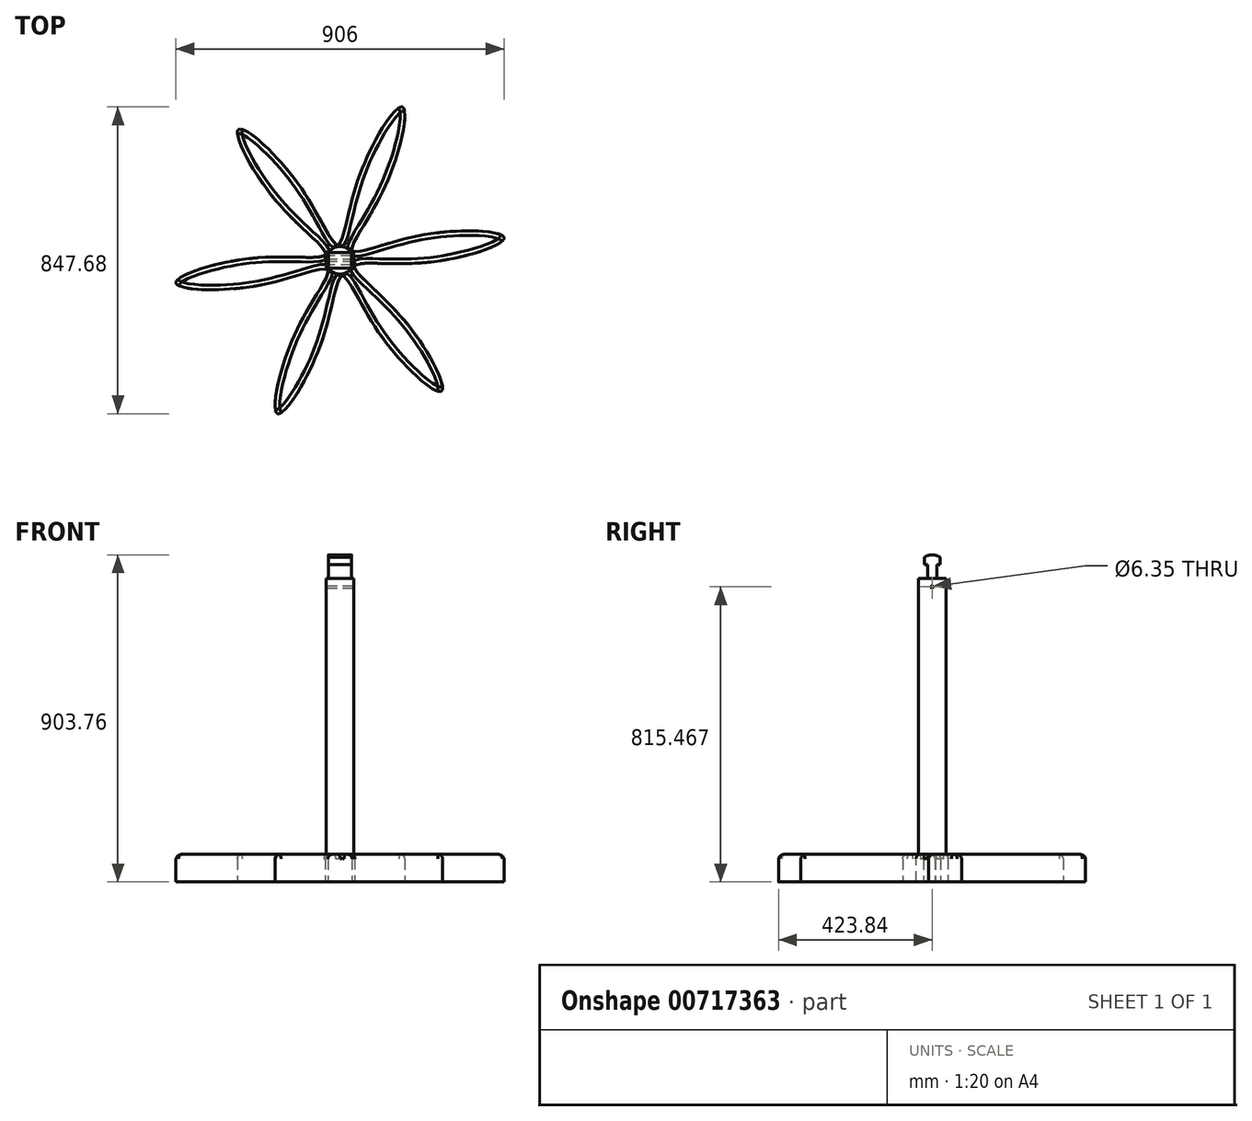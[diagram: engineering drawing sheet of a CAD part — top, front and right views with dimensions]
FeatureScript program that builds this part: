
annotation { "Feature Type Name" : "Feature", "Feature Type Description" : "" }
export const myFeature = defineFeature(function(context is Context, id is Id, definition is map)
    precondition{}
    {
        {
            var Q0;
            Q0=qCreatedBy(makeId("Top.planeOp"),FACE);
            var sketch = newSketch(context, id + "F0", { "sketchPlane" : qUnion([Q0])});
            skCircle(sketch, "E0", {"center": v(0, 0) * mm, "radius": 38.1 * mm});
            skSolve(sketch);
        }
        {
            var Q0;
            Q0=makeQuery(id+"F0.imprint","IMPRINT",FACE,{"disambiguationData":[TD([[makeQuery(id+"F0.imprint","IMPRINT",EDGE,{"derivedFrom":sQuery(id+"F0.wireOp",EDGE,"E0")}),1.0]])]});
            extrude(context, id + "F1", {"entities" : qUnion([Q0]), "depth" : 762 * mm, "offsetDistance" : 25.4 * mm});
        }
        {
            var Q0;
            Q0=makeQuery(id+"F1.opExtrude","CAP_FACE",FACE,{"disambiguationData":[OSD([sQuery(id+"F0.wireOp",EDGE,"E0")])],"isStart":false});
            var sketch = newSketch(context, id + "F2", { "sketchPlane" : qUnion([Q0])});
            skLineSegment(sketch, "E1", {"start": v(-31.75, 21.06) * mm, "end": v(-31.75, -21.06) * mm, "construction": true});
            skLineSegment(sketch, "E2", {"start": v(31.75, 21.06) * mm, "end": v(31.75, -21.06) * mm, "construction": true});
            skLineSegment(sketch, "E3", {"start": v(-31.9, 50.8) * mm, "end": v(-31.75, -50.8) * mm});
            skLineSegment(sketch, "E4", {"start": v(31.91, 50.8) * mm, "end": v(31.91, -50.8) * mm});
            skLineSegment(sketch, "E5", {"start": v(-31.9, 50.8) * mm, "end": v(31.91, 50.8) * mm});
            skLineSegment(sketch, "E6", {"start": v(31.91, -50.8) * mm, "end": v(-31.75, -50.8) * mm});
            skSolve(sketch);
        }
        {
            var Q0;
            {var subQ0=sQuery(id+"F2.wireOp",EDGE,"E5");var subQ1=sQuery(id+"F2.wireOp",EDGE,"E3");var subQ2=makeQuery(id+"F2.imprint","INTERSECT",VERTEX,{"derivedFrom":[subQ1,subQ0]});Q0=makeQuery(id+"F2.imprint","IMPRINT",FACE,{"disambiguationData":[TD([[makeQuery(id+"F2.imprint","IMPRINT",EDGE,{"disambiguationData":[TD([[subQ2,-1.0]])],"derivedFrom":subQ1}),1.0]])]});}
            var Q1;
            {var subQ0=sQuery(id+"F2.wireOp",EDGE,"E5");var subQ1=sQuery(id+"F2.wireOp",EDGE,"E4");var subQ2=makeQuery(id+"F2.imprint","INTERSECT",VERTEX,{"derivedFrom":[subQ1,subQ0]});Q1=makeQuery(id+"F2.imprint","IMPRINT",FACE,{"disambiguationData":[TD([[makeQuery(id+"F2.imprint","IMPRINT",EDGE,{"disambiguationData":[TD([[subQ2,-1.0]])],"derivedFrom":subQ1}),-1.0]])]});}
            var Q2;
            {var subQ1=makeQuery(id+"F1.opExtrude","CAP_EDGE",EDGE,{"disambiguationData":[OSD([sQuery(id+"F0.wireOp",EDGE,"E0")])],"isStart":false});var subQ7=sQuery(id+"F2.wireOp",EDGE,"E3");var subQ8=makeQuery(id+"F2.imprint","INTERSECT",VERTEX,{"disambiguationData":[OD(0.0)],"derivedFrom":[subQ1,subQ7]});Q2=makeQuery(id+"F2.imprint","IMPRINT",FACE,{"disambiguationData":[TD([[makeQuery(id+"F2.imprint","IMPRINT",EDGE,{"disambiguationData":[TD([[subQ8,-1.0]])],"derivedFrom":subQ7}),1.0]])]});}
            var Q3;
            {var subQ0=sQuery(id+"F2.wireOp",EDGE,"E6");var subQ1=sQuery(id+"F2.wireOp",EDGE,"E3");var subQ2=makeQuery(id+"F2.imprint","INTERSECT",VERTEX,{"derivedFrom":[subQ1,subQ0]});Q3=makeQuery(id+"F2.imprint","IMPRINT",FACE,{"disambiguationData":[TD([[makeQuery(id+"F2.imprint","IMPRINT",EDGE,{"disambiguationData":[TD([[subQ2,1.0]])],"derivedFrom":subQ1}),1.0]])]});}
            var Q4;
            {var subQ0=sQuery(id+"F2.wireOp",EDGE,"E6");var subQ1=sQuery(id+"F2.wireOp",EDGE,"E4");var subQ2=makeQuery(id+"F2.imprint","INTERSECT",VERTEX,{"derivedFrom":[subQ1,subQ0]});Q4=makeQuery(id+"F2.imprint","IMPRINT",FACE,{"disambiguationData":[TD([[makeQuery(id+"F2.imprint","IMPRINT",EDGE,{"disambiguationData":[TD([[subQ2,1.0]])],"derivedFrom":subQ1}),-1.0]])]});}
            extrude(context, id + "F3", {"entities" : qUnion([Q0, Q1, Q2, Q3, Q4]), "operationType" : NewBodyOperationType.ADD, "depth" : 101.6 * mm, "offsetDistance" : 25.4 * mm});
        }
        {
            var Q0;
            Q0=makeQuery(id+"F3.opExtrude","SWEPT_FACE",FACE,{"disambiguationData":[OSD([sQuery(id+"F2.wireOp",EDGE,"E3")])]});
            var sketch = newSketch(context, id + "F4", { "sketchPlane" : qUnion([Q0])});
            skLineSegment(sketch, "E7", {"start": v(-12.75, 762) * mm, "end": v(12.65, 762) * mm, "construction": true});
            skLineSegment(sketch, "E8", {"start": v(-12.75, 762) * mm, "end": v(-12.75, 800.1) * mm});
            skLineSegment(sketch, "E9", {"start": v(12.65, 762) * mm, "end": v(12.65, 800.1) * mm});
            skLineSegment(sketch, "E10", {"start": v(-12.75, 800.1) * mm, "end": v(-38.15, 800.1) * mm});
            skLineSegment(sketch, "E11", {"start": v(12.65, 800.1) * mm, "end": v(38.05, 800.1) * mm});
            skArc(sketch, "E12", {"start": v(38.05, 800.1) * mm, "mid": v(-0.05, 827.56) * mm, "end": v(-38.15, 800.1) * mm});
            skLineSegment(sketch, "E13", {"start": v(-12.75, 762) * mm, "end": v(-63.55, 762) * mm});
            skLineSegment(sketch, "E14", {"start": v(12.65, 762) * mm, "end": v(63.45, 762) * mm});
            skLineSegment(sketch, "E15", {"start": v(-63.55, 762) * mm, "end": v(-63.55, 838.2) * mm});
            skLineSegment(sketch, "E16", {"start": v(63.45, 762) * mm, "end": v(63.45, 838.2) * mm});
            skLineSegment(sketch, "E17", {"start": v(-63.55, 838.2) * mm, "end": v(63.45, 838.2) * mm});
            skSolve(sketch);
        }
        {
            var Q0;
            {var subQ8=sQuery(id+"F4.wireOp",EDGE,"E8");Q0=makeQuery(id+"F4.imprint","IMPRINT",FACE,{"disambiguationData":[TD([[makeQuery(id+"F4.imprint","IMPRINT",EDGE,{"derivedFrom":subQ8}),1.0]])]});}
            extrude(context, id + "F5", {"entities" : qUnion([Q0]), "operationType" : NewBodyOperationType.REMOVE, "oppositeDirection" : true, "depth" : 76.2 * mm, "offsetDistance" : 25.4 * mm});
        }
        {
            var Q0;
            Q0=makeQuery(id+"F3.opExtrude","SWEPT_FACE",FACE,{"disambiguationData":[OSD([sQuery(id+"F2.wireOp",EDGE,"E6")])]});
            extrude(context, id + "F6", {"entities" : qUnion([Q0]), "operationType" : NewBodyOperationType.REMOVE, "oppositeDirection" : true, "depth" : 6.35 * mm, "offsetDistance" : 25.4 * mm});
        }
        {
            var Q0;
            Q0=makeQuery(id+"F5.boolean.opBoolean","SPLIT",FACE,{"disambiguationData":[TD([makeQuery(id+"F1.opExtrude","CAP_FACE",FACE,{"disambiguationData":[OSD([sQuery(id+"F0.wireOp",EDGE,"E0")])],"isStart":false})])],"derivedFrom":makeQuery(id+"F3.opExtrude","SWEPT_FACE",FACE,{"disambiguationData":[OSD([sQuery(id+"F2.wireOp",EDGE,"E4")])]})});
            var sketch = newSketch(context, id + "F7", { "sketchPlane" : qUnion([Q0])});
            skLineSegment(sketch, "E18", {"start": v(21.7, 821.26) * mm, "end": v(21.7, 800.1) * mm});
            skLineSegment(sketch, "E19", {"start": v(-21.49, 821.26) * mm, "end": v(-21.49, 800.1) * mm, "construction": true});
            skLineSegment(sketch, "E20.bottom", {"start": v(-21.62, 960.65) * mm, "end": v(-49.27, 960.65) * mm});
            skLineSegment(sketch, "E20.top", {"start": v(-21.62, 921.94) * mm, "end": v(-49.27, 921.94) * mm});
            skLineSegment(sketch, "E20.left", {"start": v(-21.62, 960.65) * mm, "end": v(-21.62, 921.94) * mm});
            skLineSegment(sketch, "E20.right", {"start": v(-49.27, 960.65) * mm, "end": v(-49.27, 921.94) * mm});
            skSolve(sketch);
        }
        {
            var Q0;
            {var subQ8=sQuery(id+"F7.wireOp",EDGE,"E20.bottom");Q0=makeQuery(id+"F7.imprint","IMPRINT",FACE,{"disambiguationData":[TD([[makeQuery(id+"F7.imprint","IMPRINT",EDGE,{"derivedFrom":subQ8}),1.0]])]});}
            var Q1;
            {var subQ0=sQuery(id+"F7.wireOp",EDGE,"E20.left");var subQ1=makeQuery(id+"F3.opExtrude","SWEPT_FACE",FACE,{"disambiguationData":[OSD([sQuery(id+"F2.wireOp",EDGE,"E4")])]});var subQ2=makeQuery(id+"F5.boolean.opBoolean","INTERSECT",EDGE,{"derivedFrom":[subQ1,makeQuery(id+"F5.opExtrude","SWEPT_FACE",FACE,{"disambiguationData":[OSD([sQuery(id+"F4.wireOp",EDGE,"E12")])]})]});var subQ3=makeQuery(id+"F7.imprint","INTERSECT",VERTEX,{"derivedFrom":[subQ2,subQ0]});Q1=makeQuery(id+"F7.imprint","IMPRINT",FACE,{"disambiguationData":[TD([[makeQuery(id+"F7.imprint","IMPRINT",EDGE,{"disambiguationData":[TD([[subQ3,-1.0]])],"derivedFrom":subQ0}),-1.0]])]});}
            var Q2;
            {var subQ0=sQuery(id+"F7.wireOp",EDGE,"E18");Q2=makeQuery(id+"F7.imprint","IMPRINT",FACE,{"disambiguationData":[TD([[makeQuery(id+"F7.imprint","IMPRINT",EDGE,{"derivedFrom":subQ0}),1.0]])]});}
            extrude(context, id + "F8", {"entities" : qUnion([Q0, Q1, Q2]), "operationType" : NewBodyOperationType.REMOVE, "oppositeDirection" : true, "depth" : 127 * mm, "offsetDistance" : 25.4 * mm});
        }
        {
            var Q0;
            {var subQ0=sQuery(id+"F0.wireOp",EDGE,"E0");var subQ2=sQuery(id+"F2.wireOp",EDGE,"E4");var subQ3=sQuery(id+"F2.wireOp",EDGE,"E3");var subQ5=makeQuery(id+"F1.opExtrude","CAP_FACE",FACE,{"disambiguationData":[OSD([subQ0])],"isStart":false});Q0=makeQuery(id+"F5.boolean.opBoolean","MERGE",FACE,{"derivedFrom":[makeQuery(id+"F3.boolean.opBoolean","SPLIT",FACE,{"disambiguationData":[TD([makeQuery(id+"F3.opExtrude","SWEPT_FACE",FACE,{"disambiguationData":[OSD([subQ3])]})])],"derivedFrom":subQ5}),makeQuery(id+"F3.boolean.opBoolean","SPLIT",FACE,{"disambiguationData":[TD([makeQuery(id+"F3.opExtrude","SWEPT_FACE",FACE,{"disambiguationData":[OSD([subQ2])]})])],"derivedFrom":subQ5}),makeQuery(id+"F5.opExtrude","SWEPT_FACE",FACE,{"disambiguationData":[OSD([sQuery(id+"F4.wireOp",EDGE,"E13")])]}),makeQuery(id+"F5.opExtrude","SWEPT_FACE",FACE,{"disambiguationData":[OSD([sQuery(id+"F4.wireOp",EDGE,"E14")])]})]});}
            var sketch = newSketch(context, id + "F9", { "sketchPlane" : qUnion([Q0])});
            skLineSegment(sketch, "E21", {"start": v(31.91, 0.1) * mm, "end": v(38.1, 0.1) * mm, "construction": true});
            skLineSegment(sketch, "E22", {"start": v(38.1, 0.1) * mm, "end": v(37.97, 3.18) * mm, "construction": true});
            skLineSegment(sketch, "E23", {"start": v(37.97, 3.18) * mm, "end": v(37.97, -3.18) * mm, "construction": true});
            skLineSegment(sketch, "E24.bottom", {"start": v(37.97, -3.18) * mm, "end": v(36.95, -3.18) * mm});
            skLineSegment(sketch, "E24.top", {"start": v(37.97, 3.18) * mm, "end": v(36.95, 3.18) * mm});
            skLineSegment(sketch, "E24.left", {"start": v(37.97, -3.18) * mm, "end": v(37.97, 3.18) * mm});
            skLineSegment(sketch, "E24.right", {"start": v(36.95, -3.18) * mm, "end": v(36.95, 3.18) * mm});
            skLineSegment(sketch, "E25.bottom", {"start": v(36.95, -3.18) * mm, "end": v(40.28, -3.18) * mm});
            skLineSegment(sketch, "E25.top", {"start": v(36.95, 3.18) * mm, "end": v(40.28, 3.18) * mm});
            skLineSegment(sketch, "E25.right", {"start": v(40.28, -3.17) * mm, "end": v(40.28, 3.17) * mm});
            skSolve(sketch);
        }
        {
            var Q0;
            {var subQ0=sQuery(id+"F9.wireOp",EDGE,"E24.left");Q0=makeQuery(id+"F9.imprint","IMPRINT",FACE,{"disambiguationData":[TD([[makeQuery(id+"F9.imprint","IMPRINT",EDGE,{"derivedFrom":subQ0}),1.0]])]});}
            var Q1;
            {var subQ0=sQuery(id+"F9.wireOp",EDGE,"E24.left");Q1=makeQuery(id+"F9.imprint","IMPRINT",FACE,{"disambiguationData":[TD([[makeQuery(id+"F9.imprint","IMPRINT",EDGE,{"derivedFrom":subQ0}),-1.0]])]});}
            var Q2;
            {var subQ11=sQuery(id+"F9.wireOp",EDGE,"E25.right");Q2=makeQuery(id+"F9.imprint","IMPRINT",FACE,{"disambiguationData":[TD([[makeQuery(id+"F9.imprint","IMPRINT",EDGE,{"derivedFrom":subQ11}),1.0]])]});}
            extrude(context, id + "F10", {"entities" : qUnion([Q0, Q1, Q2]), "operationType" : NewBodyOperationType.REMOVE, "oppositeDirection" : true, "depth" : 25.9 * mm, "offsetDistance" : 25.4 * mm});
        }
        {
            var Q0;
            Q0=makeQuery(id+"F10.boolean.opBoolean","COPY",FACE,{"derivedFrom":makeQuery(id+"F10.opExtrude","SWEPT_FACE",FACE,{"disambiguationData":[OSD([sQuery(id+"F9.wireOp",EDGE,"E24.right")])]})});
            var sketch = newSketch(context, id + "F11", { "sketchPlane" : qUnion([Q0])});
            skLineSegment(sketch, "E26", {"start": v(0, 736.1) * mm, "end": v(0, 739.27) * mm, "construction": true});
            skCircle(sketch, "E27", {"center": v(0, 739.27) * mm, "radius": 3.18 * mm});
            skSolve(sketch);
        }
        {
            var Q0;
            {var subQ0=sQuery(id+"F11.wireOp",EDGE,"E27");var subQ1=sQuery(id+"F9.wireOp",EDGE,"E24.right");var subQ4=makeQuery(id+"F11.imprint","INTERSECT",VERTEX,{"derivedFrom":[makeQuery(id+"F10.boolean.opBoolean","COPY",EDGE,{"derivedFrom":makeQuery(id+"F10.opExtrude","CAP_EDGE",EDGE,{"disambiguationData":[OSD([subQ1])],"isStart":false})}),subQ0]});Q0=makeQuery(id+"F11.imprint","IMPRINT",FACE,{"disambiguationData":[TD([[makeQuery(id+"F11.imprint","IMPRINT",EDGE,{"disambiguationData":[TD([[subQ4,1.0]])],"derivedFrom":subQ0}),1.0]])]});}
            extrude(context, id + "F12", {"entities" : qUnion([Q0]), "operationType" : NewBodyOperationType.REMOVE, "oppositeDirection" : true, "depth" : 101.6 * mm, "offsetDistance" : 25.4 * mm});
        }
        {
            var Q0;
            Q0=makeQuery(id+"F1.opExtrude","CAP_FACE",FACE,{"disambiguationData":[OSD([sQuery(id+"F0.wireOp",EDGE,"E0")])],"isStart":true});
            var sketch = newSketch(context, id + "F13", { "sketchPlane" : qUnion([Q0])});
            skLineSegment(sketch, "E28", {"start": v(21.92, -31.16) * mm, "end": v(21.92, 31.16) * mm});
            skSolve(sketch);
        }
        {
            var Q0;
            {var subQ0=sQuery(id+"F13.wireOp",EDGE,"E28");Q0=makeQuery(id+"F13.imprint","IMPRINT",FACE,{"disambiguationData":[TD([[makeQuery(id+"F13.imprint","IMPRINT",EDGE,{"derivedFrom":subQ0}),-1.0]])]});}
            extrude(context, id + "F14", {"entities" : qUnion([Q0]), "operationType" : NewBodyOperationType.ADD, "oppositeDirection" : true, "depth" : 762 * mm, "offsetDistance" : 25.4 * mm});
        }
        {
            var Q0;
            Q0=makeQuery(id+"F14.opExtrude","SWEPT_FACE",FACE,{"disambiguationData":[OSD([sQuery(id+"F13.wireOp",EDGE,"E28")])]});
            extrude(context, id + "F15", {"entities" : qUnion([Q0]), "operationType" : NewBodyOperationType.REMOVE, "oppositeDirection" : true, "depth" : 76.2 * mm, "offsetDistance" : 25.4 * mm});
        }
        {
            var Q0;
            Q0=makeQuery(id+"F5.boolean.opBoolean","SPLIT",FACE,{"disambiguationData":[TD([makeQuery(id+"F1.opExtrude","CAP_FACE",FACE,{"disambiguationData":[OSD([sQuery(id+"F0.wireOp",EDGE,"E0")])],"isStart":false})])],"derivedFrom":makeQuery(id+"F3.opExtrude","SWEPT_FACE",FACE,{"disambiguationData":[OSD([sQuery(id+"F2.wireOp",EDGE,"E4")])]})});
            var sketch = newSketch(context, id + "F16", { "sketchPlane" : qUnion([Q0])});
            skLineSegment(sketch, "E29", {"start": v(21.7, 821.26) * mm, "end": v(-21.49, 821.26) * mm, "construction": true});
            skLineSegment(sketch, "E30.bottom", {"start": v(-21.57, 828.07) * mm, "end": v(-42.3, 828.07) * mm, "construction": true});
            skLineSegment(sketch, "E30.top", {"start": v(-21.57, 792.23) * mm, "end": v(-42.3, 792.23) * mm, "construction": true});
            skLineSegment(sketch, "E30.left", {"start": v(-21.57, 828.07) * mm, "end": v(-21.57, 792.23) * mm, "construction": true});
            skLineSegment(sketch, "E30.right", {"start": v(-42.3, 828.07) * mm, "end": v(-42.3, 792.23) * mm, "construction": true});
            skLineSegment(sketch, "E31.bottom", {"start": v(-21.57, 828.07) * mm, "end": v(-42.3, 828.07) * mm});
            skLineSegment(sketch, "E31.top", {"start": v(-21.57, 792.23) * mm, "end": v(-42.3, 792.23) * mm});
            skLineSegment(sketch, "E31.left", {"start": v(-21.57, 828.07) * mm, "end": v(-21.57, 792.23) * mm});
            skLineSegment(sketch, "E31.right", {"start": v(-42.3, 828.07) * mm, "end": v(-42.3, 792.23) * mm});
            skLineSegment(sketch, "E32.bottom", {"start": v(-57.93, 875.38) * mm, "end": v(59.9, 875.38) * mm});
            skLineSegment(sketch, "E32.top", {"start": v(-57.93, 833.25) * mm, "end": v(59.9, 833.25) * mm});
            skLineSegment(sketch, "E32.left", {"start": v(-57.93, 875.38) * mm, "end": v(-57.93, 833.25) * mm});
            skLineSegment(sketch, "E32.right", {"start": v(59.9, 875.38) * mm, "end": v(59.9, 833.25) * mm});
            skSolve(sketch);
        }
        {
            var Q0;
            Q0=makeQuery(id+"F16.imprint","IMPRINT",FACE,{"disambiguationData":[TD([[makeQuery(id+"F16.imprint","IMPRINT",EDGE,{"derivedFrom":sQuery(id+"F16.wireOp",EDGE,"E32.bottom")}),-1.0]])]});
            var Q1;
            {var subQ5=sQuery(id+"F16.wireOp",EDGE,"E31.bottom");Q1=makeQuery(id+"F16.imprint","IMPRINT",FACE,{"disambiguationData":[TD([[makeQuery(id+"F16.imprint","IMPRINT",EDGE,{"derivedFrom":subQ5}),1.0]])]});}
            var Q2;
            {var subQ0=sQuery(id+"F16.wireOp",EDGE,"E31.left");var subQ1=makeQuery(id+"F3.opExtrude","SWEPT_FACE",FACE,{"disambiguationData":[OSD([sQuery(id+"F2.wireOp",EDGE,"E4")])]});var subQ2=makeQuery(id+"F5.boolean.opBoolean","INTERSECT",EDGE,{"derivedFrom":[subQ1,makeQuery(id+"F5.opExtrude","SWEPT_FACE",FACE,{"disambiguationData":[OSD([sQuery(id+"F4.wireOp",EDGE,"E12")])]})]});var subQ3=makeQuery(id+"F16.imprint","INTERSECT",VERTEX,{"derivedFrom":[subQ2,subQ0]});Q2=makeQuery(id+"F16.imprint","IMPRINT",FACE,{"disambiguationData":[TD([[makeQuery(id+"F16.imprint","IMPRINT",EDGE,{"disambiguationData":[TD([[subQ3,-1.0]])],"derivedFrom":subQ0}),-1.0]])]});}
            extrude(context, id + "F17", {"entities" : qUnion([Q0, Q1, Q2]), "operationType" : NewBodyOperationType.REMOVE, "oppositeDirection" : true, "depth" : 127 * mm, "offsetDistance" : 25.4 * mm});
        }
        {
            var Q0;
            Q0=makeQuery(id+"F1.opExtrude","CAP_FACE",FACE,{"disambiguationData":[OSD([sQuery(id+"F0.wireOp",EDGE,"E0")])],"isStart":true});
            var sketch = newSketch(context, id + "F18", { "sketchPlane" : qUnion([Q0])});
            skCircle(sketch, "E33.cCircle", {"center": v(0, 0) * mm, "radius": 38.1 * mm, "construction": true});
            skLineSegment(sketch, "E33.0", {"start": v(34.75, -26.98) * mm, "end": v(-6, -43.58) * mm});
            skLineSegment(sketch, "E33.1", {"start": v(-6, -43.58) * mm, "end": v(-40.74, -16.6) * mm});
            skLineSegment(sketch, "E33.2", {"start": v(-40.74, -16.6) * mm, "end": v(-34.75, 26.98) * mm});
            skLineSegment(sketch, "E33.3", {"start": v(-34.75, 26.98) * mm, "end": v(6, 43.58) * mm});
            skLineSegment(sketch, "E33.4", {"start": v(6, 43.58) * mm, "end": v(40.74, 16.6) * mm});
            skLineSegment(sketch, "E33.5", {"start": v(40.74, 16.6) * mm, "end": v(34.75, -26.98) * mm});
            skPoint(sketch, "E33.0.midPoint", {"position": v(14.38, -35.28) * mm});
            skSolve(sketch);
        }
        {
            var Q0;
            {var subQ0=sQuery(id+"F18.wireOp",EDGE,"E33.3");var subQ1=sQuery(id+"F18.wireOp",EDGE,"E33.2");var subQ2=makeQuery(id+"F18.imprint","INTERSECT",VERTEX,{"derivedFrom":[subQ1,subQ0]});Q0=makeQuery(id+"F18.imprint","IMPRINT",FACE,{"disambiguationData":[TD([[makeQuery(id+"F18.imprint","IMPRINT",EDGE,{"disambiguationData":[TD([[subQ2,1.0]])],"derivedFrom":subQ1}),-1.0]])]});}
            var Q1;
            {var subQ0=sQuery(id+"F18.wireOp",EDGE,"E33.2");var subQ1=sQuery(id+"F18.wireOp",EDGE,"E33.1");var subQ2=makeQuery(id+"F18.imprint","INTERSECT",VERTEX,{"derivedFrom":[subQ1,subQ0]});Q1=makeQuery(id+"F18.imprint","IMPRINT",FACE,{"disambiguationData":[TD([[makeQuery(id+"F18.imprint","IMPRINT",EDGE,{"disambiguationData":[TD([[subQ2,1.0]])],"derivedFrom":subQ1}),-1.0]])]});}
            var Q2;
            {var subQ0=makeQuery(id+"F1.opExtrude","CAP_EDGE",EDGE,{"disambiguationData":[OSD([sQuery(id+"F0.wireOp",EDGE,"E0")])],"isStart":true});var subQ4=makeQuery(id+"F18.imprint","INTERSECT",VERTEX,{"derivedFrom":[subQ0,sQuery(id+"F18.wireOp",EDGE,"E33.0")]});Q2=makeQuery(id+"F18.imprint","IMPRINT",FACE,{"disambiguationData":[TD([[makeQuery(id+"F18.imprint","IMPRINT",EDGE,{"disambiguationData":[TD([[subQ4,-1.0]])],"derivedFrom":subQ0}),-1.0]])]});}
            var Q3;
            {var subQ0=sQuery(id+"F18.wireOp",EDGE,"E33.4");var subQ1=sQuery(id+"F18.wireOp",EDGE,"E33.3");var subQ2=makeQuery(id+"F18.imprint","INTERSECT",VERTEX,{"derivedFrom":[subQ1,subQ0]});Q3=makeQuery(id+"F18.imprint","IMPRINT",FACE,{"disambiguationData":[TD([[makeQuery(id+"F18.imprint","IMPRINT",EDGE,{"disambiguationData":[TD([[subQ2,1.0]])],"derivedFrom":subQ1}),-1.0]])]});}
            var Q4;
            {var subQ0=sQuery(id+"F18.wireOp",EDGE,"E33.5");var subQ1=sQuery(id+"F18.wireOp",EDGE,"E33.4");var subQ2=makeQuery(id+"F18.imprint","INTERSECT",VERTEX,{"derivedFrom":[subQ1,subQ0]});Q4=makeQuery(id+"F18.imprint","IMPRINT",FACE,{"disambiguationData":[TD([[makeQuery(id+"F18.imprint","IMPRINT",EDGE,{"disambiguationData":[TD([[subQ2,1.0]])],"derivedFrom":subQ1}),-1.0]])]});}
            var Q5;
            {var subQ0=sQuery(id+"F18.wireOp",EDGE,"E33.5");var subQ1=sQuery(id+"F18.wireOp",EDGE,"E33.0");var subQ2=makeQuery(id+"F18.imprint","INTERSECT",VERTEX,{"derivedFrom":[subQ1,subQ0]});Q5=makeQuery(id+"F18.imprint","IMPRINT",FACE,{"disambiguationData":[TD([[makeQuery(id+"F18.imprint","IMPRINT",EDGE,{"disambiguationData":[TD([[subQ2,-1.0]])],"derivedFrom":subQ1}),-1.0]])]});}
            var Q6;
            {var subQ0=sQuery(id+"F18.wireOp",EDGE,"E33.1");var subQ1=sQuery(id+"F18.wireOp",EDGE,"E33.0");var subQ2=makeQuery(id+"F18.imprint","INTERSECT",VERTEX,{"derivedFrom":[subQ1,subQ0]});Q6=makeQuery(id+"F18.imprint","IMPRINT",FACE,{"disambiguationData":[TD([[makeQuery(id+"F18.imprint","IMPRINT",EDGE,{"disambiguationData":[TD([[subQ2,1.0]])],"derivedFrom":subQ1}),-1.0]])]});}
            extrude(context, id + "F19", {"entities" : qUnion([Q0, Q1, Q2, Q3, Q4, Q5, Q6]), "operationType" : NewBodyOperationType.ADD, "depth" : 76.2 * mm, "offsetDistance" : 25.4 * mm});
        }
        {
            var Q0;
            Q0=makeQuery(id+"F19.opExtrude","CAP_FACE",FACE,{"disambiguationData":[OSD([sQuery(id+"F18.wireOp",EDGE,"E33.0"),sQuery(id+"F18.wireOp",EDGE,"E33.1"),sQuery(id+"F18.wireOp",EDGE,"E33.2"),sQuery(id+"F18.wireOp",EDGE,"E33.3"),sQuery(id+"F18.wireOp",EDGE,"E33.4"),sQuery(id+"F18.wireOp",EDGE,"E33.5")])],"isStart":false});
            var sketch = newSketch(context, id + "F20", { "sketchPlane" : qUnion([Q0])});
            skLineSegment(sketch, "E34", {"start": v(0, 0) * mm, "end": v(-452.94, 62.26) * mm, "construction": true});
            skLineSegment(sketch, "E35", {"start": v(0, 0) * mm, "end": v(452.94, -62.26) * mm, "construction": true});
            skLineSegment(sketch, "E36", {"start": v(0, 0) * mm, "end": v(280.4, 361.13) * mm, "construction": true});
            skLineSegment(sketch, "E37", {"start": v(0, 0) * mm, "end": v(-172.55, 423.39) * mm, "construction": true});
            skLineSegment(sketch, "E38", {"start": v(0, 0) * mm, "end": v(172.55, -423.39) * mm, "construction": true});
            skLineSegment(sketch, "E39", {"start": v(0, 0) * mm, "end": v(-280.4, -361.13) * mm, "construction": true});
            skLineSegment(sketch, "E40", {"start": v(-86.27, 211.7) * mm, "end": v(-51, 226.07) * mm, "construction": true});
            skLineSegment(sketch, "E41", {"start": v(-86.27, 211.7) * mm, "end": v(-121.56, 197.32) * mm, "construction": true});
            skLineSegment(sketch, "E42", {"start": v(-226.47, 31.13) * mm, "end": v(-221.28, 68.88) * mm, "construction": true});
            skLineSegment(sketch, "E43", {"start": v(-226.47, 31.13) * mm, "end": v(-231.66, -6.61) * mm, "construction": true});
            skLineSegment(sketch, "E44", {"start": v(-140.2, -180.56) * mm, "end": v(-170.3, -157.2) * mm, "construction": true});
            skLineSegment(sketch, "E45", {"start": v(-140.2, -180.56) * mm, "end": v(-110.1, -203.93) * mm, "construction": true});
            skLineSegment(sketch, "E46", {"start": v(86.27, -211.7) * mm, "end": v(51, -226.07) * mm, "construction": true});
            skLineSegment(sketch, "E47", {"start": v(86.27, -211.7) * mm, "end": v(121.56, -197.32) * mm, "construction": true});
            skLineSegment(sketch, "E48", {"start": v(226.47, -31.13) * mm, "end": v(221.28, -68.88) * mm, "construction": true});
            skLineSegment(sketch, "E49", {"start": v(226.47, -31.13) * mm, "end": v(231.66, 6.61) * mm, "construction": true});
            skLineSegment(sketch, "E50", {"start": v(140.2, 180.56) * mm, "end": v(170.3, 157.2) * mm, "construction": true});
            skLineSegment(sketch, "E51", {"start": v(140.2, 180.56) * mm, "end": v(110.1, 203.93) * mm, "construction": true});
            skFitSpline(sketch, "E52", {"points": [v(-172.55, 423.39) * mm, v(-51, 226.07) * mm, v(6, 43.58) * mm, v(110.1, 203.93) * mm, v(280.4, 361.13) * mm, v(170.3, 157.2) * mm, v(40.74, 16.6) * mm, v(231.66, 6.61) * mm, v(452.94, -62.26) * mm, v(221.28, -68.88) * mm, v(34.75, -26.98) * mm, v(121.56, -197.32) * mm, v(172.55, -423.39) * mm, v(51, -226.07) * mm, v(-6, -43.58) * mm, v(-110.1, -203.93) * mm, v(-280.4, -361.13) * mm, v(-170.3, -157.2) * mm, v(-40.74, -16.6) * mm, v(-231.66, -6.61) * mm, v(-452.94, 62.26) * mm, v(-221.28, 68.88) * mm, v(-34.75, 26.98) * mm, v(-121.56, 197.32) * mm, v(-172.55, 423.39) * mm]});
            skSolve(sketch);
        }
        {
            var Q0;
            {var subQ1=makeQuery(id+"F19.opExtrude","CAP_EDGE",EDGE,{"disambiguationData":[OSD([sQuery(id+"F18.wireOp",EDGE,"E33.3")])],"isStart":false});Q0=makeQuery(id+"F20.imprint","IMPRINT",FACE,{"disambiguationData":[TD([[makeQuery(id+"F20.imprint","IMPRINT",EDGE,{"derivedFrom":subQ1}),1.0]])]});}
            var Q1;
            {var subQ1=makeQuery(id+"F19.opExtrude","CAP_EDGE",EDGE,{"disambiguationData":[OSD([sQuery(id+"F18.wireOp",EDGE,"E33.4")])],"isStart":false});Q1=makeQuery(id+"F20.imprint","IMPRINT",FACE,{"disambiguationData":[TD([[makeQuery(id+"F20.imprint","IMPRINT",EDGE,{"derivedFrom":subQ1}),1.0]])]});}
            var Q2;
            {var subQ1=makeQuery(id+"F19.opExtrude","CAP_EDGE",EDGE,{"disambiguationData":[OSD([sQuery(id+"F18.wireOp",EDGE,"E33.5")])],"isStart":false});Q2=makeQuery(id+"F20.imprint","IMPRINT",FACE,{"disambiguationData":[TD([[makeQuery(id+"F20.imprint","IMPRINT",EDGE,{"derivedFrom":subQ1}),1.0]])]});}
            var Q3;
            {var subQ1=makeQuery(id+"F19.opExtrude","CAP_EDGE",EDGE,{"disambiguationData":[OSD([sQuery(id+"F18.wireOp",EDGE,"E33.0")])],"isStart":false});Q3=makeQuery(id+"F20.imprint","IMPRINT",FACE,{"disambiguationData":[TD([[makeQuery(id+"F20.imprint","IMPRINT",EDGE,{"derivedFrom":subQ1}),1.0]])]});}
            var Q4;
            {var subQ1=makeQuery(id+"F19.opExtrude","CAP_EDGE",EDGE,{"disambiguationData":[OSD([sQuery(id+"F18.wireOp",EDGE,"E33.1")])],"isStart":false});Q4=makeQuery(id+"F20.imprint","IMPRINT",FACE,{"disambiguationData":[TD([[makeQuery(id+"F20.imprint","IMPRINT",EDGE,{"derivedFrom":subQ1}),1.0]])]});}
            var Q5;
            {var subQ1=makeQuery(id+"F19.opExtrude","CAP_EDGE",EDGE,{"disambiguationData":[OSD([sQuery(id+"F18.wireOp",EDGE,"E33.2")])],"isStart":false});Q5=makeQuery(id+"F20.imprint","IMPRINT",FACE,{"disambiguationData":[TD([[makeQuery(id+"F20.imprint","IMPRINT",EDGE,{"derivedFrom":subQ1}),1.0]])]});}
            extrude(context, id + "F21", {"entities" : qUnion([Q0, Q1, Q2, Q3, Q4, Q5]), "operationType" : NewBodyOperationType.ADD, "oppositeDirection" : true, "depth" : 76.2 * mm, "offsetDistance" : 25.4 * mm});
        }
        {
            var Q0;
            {var subQ0=sQuery(id+"F20.wireOp",EDGE,"E52");var subQ1=makeQuery(id+"F19.opExtrude","CAP_EDGE",EDGE,{"disambiguationData":[OSD([sQuery(id+"F18.wireOp",EDGE,"E33.3")])],"isStart":false});var subQ2=makeQuery(id+"F19.opExtrude","CAP_EDGE",EDGE,{"disambiguationData":[OSD([sQuery(id+"F18.wireOp",EDGE,"E33.2")])],"isStart":false});var subQ3=makeQuery(id+"F20.imprint","INTERSECT",VERTEX,{"derivedFrom":[subQ2,subQ1,subQ0]});var subQ4=makeQuery(id+"F19.opExtrude","CAP_EDGE",EDGE,{"disambiguationData":[OSD([sQuery(id+"F18.wireOp",EDGE,"E33.4")])],"isStart":false});var subQ5=makeQuery(id+"F20.imprint","INTERSECT",VERTEX,{"derivedFrom":[subQ1,subQ4,subQ0]});var subQ6=makeQuery(id+"F19.opExtrude","CAP_EDGE",EDGE,{"disambiguationData":[OSD([sQuery(id+"F18.wireOp",EDGE,"E33.1")])],"isStart":false});var subQ7=makeQuery(id+"F20.imprint","INTERSECT",VERTEX,{"derivedFrom":[subQ6,subQ2,subQ0]});var subQ8=makeQuery(id+"F19.opExtrude","CAP_EDGE",EDGE,{"disambiguationData":[OSD([sQuery(id+"F18.wireOp",EDGE,"E33.0")])],"isStart":false});var subQ9=makeQuery(id+"F20.imprint","INTERSECT",VERTEX,{"derivedFrom":[subQ8,subQ6,subQ0]});var subQ10=makeQuery(id+"F19.opExtrude","CAP_EDGE",EDGE,{"disambiguationData":[OSD([sQuery(id+"F18.wireOp",EDGE,"E33.5")])],"isStart":false});var subQ11=makeQuery(id+"F20.imprint","INTERSECT",VERTEX,{"derivedFrom":[subQ8,subQ10,subQ0]});Q0=makeQuery(id+"F21.boolean.opBoolean","MERGE",EDGE,{"derivedFrom":[makeQuery(id+"F21.opExtrude","CAP_EDGE",EDGE,{"disambiguationData":[OSD([subQ0]),TDD([makeQuery(id+"F20.imprint","IMPRINT",EDGE,{"disambiguationData":[TD([[subQ5,-1.0]])],"derivedFrom":subQ0})])],"isStart":false}),makeQuery(id+"F21.opExtrude","CAP_EDGE",EDGE,{"disambiguationData":[OSD([subQ0]),TDD([makeQuery(id+"F20.imprint","IMPRINT",EDGE,{"disambiguationData":[TD([[subQ11,1.0]])],"derivedFrom":subQ0})])],"isStart":false}),makeQuery(id+"F21.opExtrude","CAP_EDGE",EDGE,{"disambiguationData":[OSD([subQ0]),TDD([makeQuery(id+"F20.imprint","IMPRINT",EDGE,{"disambiguationData":[TD([[subQ11,-1.0]])],"derivedFrom":subQ0})])],"isStart":false}),makeQuery(id+"F21.opExtrude","CAP_EDGE",EDGE,{"disambiguationData":[OSD([subQ0]),TDD([makeQuery(id+"F20.imprint","IMPRINT",EDGE,{"disambiguationData":[TD([[subQ9,-1.0]])],"derivedFrom":subQ0})])],"isStart":false}),makeQuery(id+"F21.opExtrude","CAP_EDGE",EDGE,{"disambiguationData":[OSD([subQ0]),TDD([makeQuery(id+"F20.imprint","IMPRINT",EDGE,{"disambiguationData":[TD([[subQ7,-1.0]])],"derivedFrom":subQ0})])],"isStart":false}),makeQuery(id+"F21.opExtrude","CAP_EDGE",EDGE,{"disambiguationData":[OSD([subQ0]),TDD([makeQuery(id+"F20.imprint","IMPRINT",EDGE,{"disambiguationData":[TD([[subQ3,-1.0]])],"derivedFrom":subQ0})])],"isStart":false})]});}
            fillet(context, id + "F22", {"entities" : qUnion([Q0]), "radius" : 12.7 * mm, "tangentPropagation" : true, "allowEdgeOverflow" : false});
        }
    });
